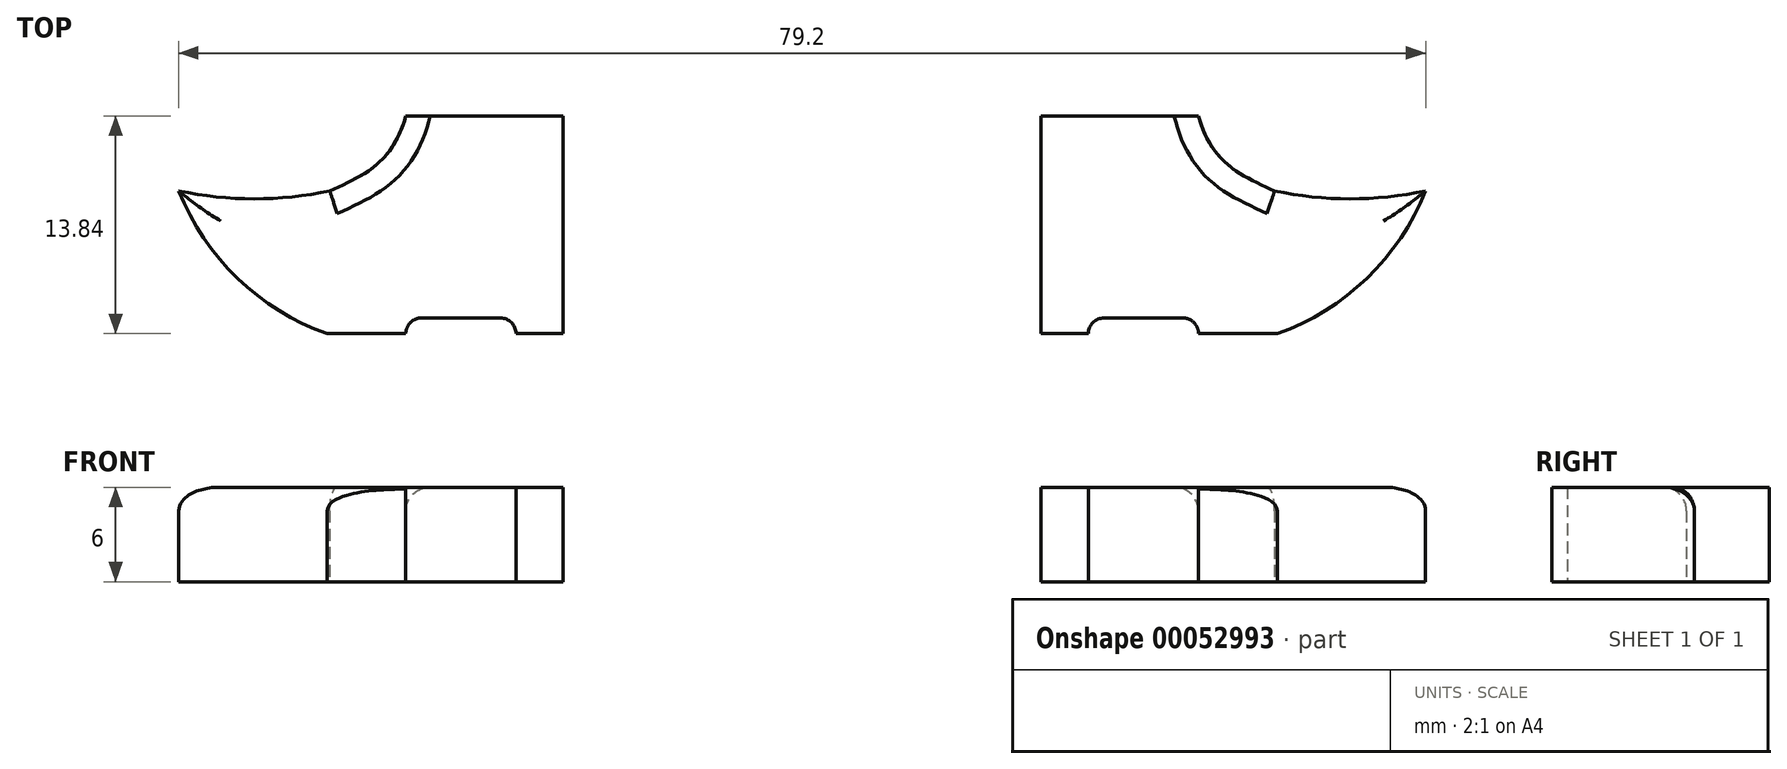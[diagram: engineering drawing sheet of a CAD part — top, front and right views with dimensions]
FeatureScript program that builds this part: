
annotation { "Feature Type Name" : "Feature", "Feature Type Description" : "" }
export const myFeature = defineFeature(function(context is Context, id is Id, definition is map)
    precondition{}
    {
        {
            var Q0;
            Q0=qCreatedBy(makeId("Top.planeOp"),FACE);
            var sketch = newSketch(context, id + "F0", { "sketchPlane" : qUnion([Q0])});
            skArc(sketch, "E0", {"start": v(-39.6, 9.07) * mm, "mid": v(-35.86, 3.52) * mm, "end": v(-30.18, 0) * mm});
            skArc(sketch, "E1", {"start": v(-39.6, 9.07) * mm, "mid": v(-34.8, 8.57) * mm, "end": v(-30, 9.07) * mm});
            skFitSpline(sketch, "E2", {"points": [v(-30, 9.07) * mm, v(-26.72, 11.03) * mm, v(-25.18, 13.84) * mm], "startDerivative": vector(7.02, 3.2) * mm, "endDerivative": vector(1.58, 6.1) * mm});
            skLineSegment(sketch, "E3", {"start": v(-25.18, 13.84) * mm, "end": v(-15.18, 13.84) * mm});
            skLineSegment(sketch, "E4", {"start": v(-15.18, 13.84) * mm, "end": v(-15.18, 0) * mm});
            skLineSegment(sketch, "E5.top", {"start": v(-19.18, 1) * mm, "end": v(-24.18, 1) * mm});
            skArc(sketch, "E6", {"start": v(-18.18, 0) * mm, "mid": v(-18.47, 0.7) * mm, "end": v(-19.18, 1) * mm});
            skArc(sketch, "E7", {"start": v(-24.18, 1) * mm, "mid": v(-24.88, 0.7) * mm, "end": v(-25.18, 0) * mm});
            skLineSegment(sketch, "E8", {"start": v(-25.18, 0) * mm, "end": v(-30.18, 0) * mm});
            skLineSegment(sketch, "E9", {"start": v(-15.18, 0) * mm, "end": v(-18.18, 0) * mm});
            skSolve(sketch);
        }
        {
            var Q0;
            Q0=qSketchRegion(id+"F0",true);
            var Q1;
            Q1=qSketchRegion(id+"F0",true);
            extrude(context, id + "F1", {"entities" : qUnion([Q0, Q1]), "depth" : 6 * mm});
        }
        {
            var Q0;
            Q0=makeQuery(id+"F1.opExtrude","CAP_EDGE",EDGE,{"disambiguationData":[OSD([sQuery(id+"F0.wireOp",EDGE,"E1")])],"isStart":false});
            var Q1;
            Q1=makeQuery(id+"F1.opExtrude","CAP_EDGE",EDGE,{"disambiguationData":[OSD([sQuery(id+"F0.wireOp",EDGE,"E0")])],"isStart":false});
            var Q2;
            Q2=makeQuery(id+"F1.opExtrude","CAP_EDGE",EDGE,{"disambiguationData":[OSD([sQuery(id+"F0.wireOp",EDGE,"E2")])],"isStart":false});
            fillet(context, id + "F2", {"entities" : qUnion([Q0, Q1, Q2]), "radius" : 1.5 * mm, "tangentPropagation" : true, "allowEdgeOverflow" : false});
        }
        {
            var Q0;
            Q0=makeQuery(id+"F1.opExtrude","SWEPT_BODY",BODY,{"disambiguationData":[OSD([sQuery(id+"F0.wireOp",EDGE,"r9N5trwQ-pjTS-P4K1-8QWj-axli2bu9RrI8"),sQuery(id+"F0.wireOp",EDGE,"E0"),sQuery(id+"F0.wireOp",EDGE,"E1"),sQuery(id+"F0.wireOp",EDGE,"E2"),sQuery(id+"F0.wireOp",EDGE,"E3"),sQuery(id+"F0.wireOp",EDGE,"E4"),sQuery(id+"F0.wireOp",EDGE,"E5.top"),sQuery(id+"F0.wireOp",EDGE,"9d063ae3-84a6-4d8e-8db5-bfca13e90d22.trimOffspring"),sQuery(id+"F0.wireOp",EDGE,"4a1767ce-735a-453f-8dc4-2587bb333832"),sQuery(id+"F0.wireOp",EDGE,"E6")])]});
            var Q1;
            Q1=qCreatedBy(makeId("Right.planeOp"),FACE);
            mirror(context, id + "F3", {"entities" : qUnion([Q0]), "mirrorPlane" : qUnion([Q1])});
        }
    });
